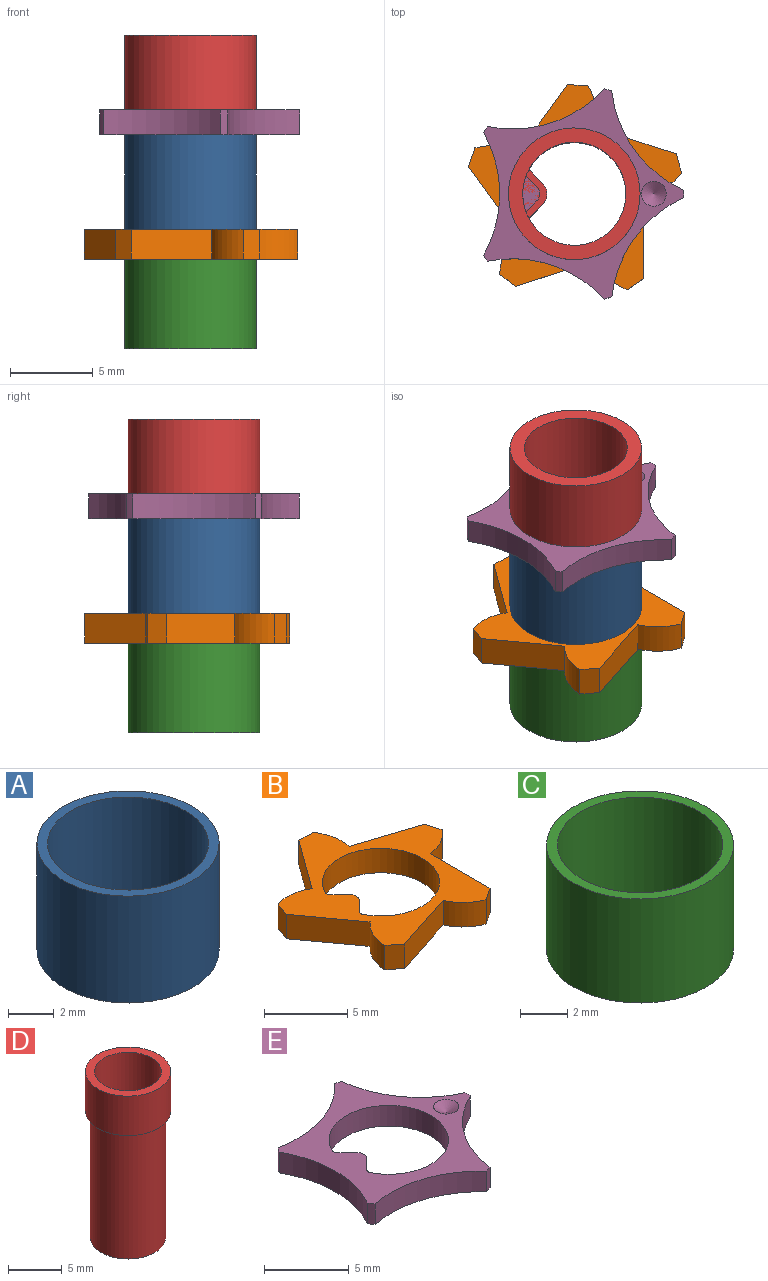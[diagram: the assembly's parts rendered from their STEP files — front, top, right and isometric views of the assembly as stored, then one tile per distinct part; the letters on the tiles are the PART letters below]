
ASSEMBLY  parts=5 mates=3
PART A: 4 faces, bbox 7.9x7.9x5.7 mm
  f0: cylinder r=3.51mm len=7.02mm, axis (0,0,-1), area 125.7mm2, adj f2,f3
  f1: cylinder r=3.97mm len=7.94mm, axis (0,0,-1), area 142.2mm2, adj f2,f3
  f2: plane 7.94x7.94mm, normal (0,0,1), area 10.8mm2, adj f0,f1
  f3: plane 7.94x7.94mm, normal (0,0,-1), area 10.8mm2, adj f0,f1
PART B: 23 faces, bbox 12.9x12.4x1.8 mm
  f0: plane 5.09x1.8mm, normal (1,0,0), area 9.2mm2, adj f1,f20,f21,f22
  f1: cylinder r=3.29mm len=2.28mm, axis (0,0,-1), area 4.8mm2, adj f0,f2,f21,f22
  f2: plane 1.8x1.15mm, normal (0.96,0.28,0), area 2.2mm2, adj f1,f3,f21,f22
  f3: plane 4.84x1.8mm, normal (0.31,0.95,0), area 9.2mm2, adj f2,f4,f21,f22
  f4: cylinder r=3.29mm len=2.56mm, axis (0,0,-1), area 4.8mm2, adj f3,f5,f21,f22
  f5: plane 1.8x1.2mm, normal (0.03,1,0), area 2.2mm2, adj f4,f6,f21,f22
  f6: plane 4.12x2.99mm, normal (-0.81,0.59,0), area 9.2mm2, adj f5,f7,f21,f22
  f7: cylinder r=3.29mm len=2.59mm, axis (0,0,-1), area 4.8mm2, adj f6,f8,f21,f22
  f8: plane 1.8x1.13mm, normal (-0.94,0.34,0), area 2.2mm2, adj f7,f9,f21,f22
  f9: plane 4.12x2.99mm, normal (-0.81,-0.59,0), area 9.2mm2, adj f8,f10,f21,f22
  f10: cylinder r=3.29mm len=2.37mm, axis (0,0,-1), area 4.8mm2, adj f9,f11,f21,f22
  f11: plane 1.8x0.95mm, normal (-0.61,-0.79,0), area 2.2mm2, adj f10,f12,f21,f22
  f12: plane 4.84x1.8mm, normal (0.31,-0.95,0), area 9.2mm2, adj f11,f13,f21,f22
  f13: cylinder r=3.29mm len=1.91mm, axis (0,0,-1), area 4.8mm2, adj f12,f20,f21,f22
  f14: cylinder r=3.53mm len=7.06mm, axis (0,0,-1), area 33.9mm2, adj f15,f19,f21,f22
  f15: cylinder r=0.3mm len=1.8mm, axis (0,0,-1), area 0.7mm2, adj f14,f16,f21,f22
  f16: plane 1.8x0.83mm, normal (0.71,-0.71,0), area 2.1mm2, adj f15,f17,f21,f22
  f17: cylinder r=0.6mm len=1.8mm, axis (0,0,-1), area 1.7mm2, adj f16,f18,f21,f22
  f18: plane 1.8x0.83mm, normal (0.71,0.71,0), area 2.1mm2, adj f17,f19,f21,f22
  f19: cylinder r=0.3mm len=1.8mm, axis (0,0,-1), area 0.7mm2, adj f14,f18,f21,f22
  f20: plane 1.8x0.99mm, normal (0.56,-0.83,0), area 2.2mm2, adj f0,f13,f21,f22
  f21: plane 12.87x12.36mm, normal (0,0,1), area 52.2mm2, adj f0,f1,f2,f3,f4,f5,f6,f7
  f22: plane 12.87x12.36mm, normal (0,0,-1), area 52.2mm2, adj f0,f1,f2,f3,f4,f5,f6,f7
PART C: 4 faces, bbox 7.9x7.9x5.4 mm
  f0: cylinder r=3.51mm len=7.02mm, axis (0,0,-1), area 119.1mm2, adj f2,f3
  f1: cylinder r=3.97mm len=7.94mm, axis (0,0,-1), area 134.7mm2, adj f2,f3
  f2: plane 7.94x7.94mm, normal (0,0,1), area 10.8mm2, adj f0,f1
  f3: plane 7.94x7.94mm, normal (0,0,-1), area 10.8mm2, adj f0,f1
PART D: 12 faces, bbox 7.9x7.9x18.9 mm
  f0: cylinder r=3.11mm len=18.9mm, axis (0,0,-1), area 321.8mm2, adj f2,f4,f6,f7,f11
  f1: cylinder r=3.97mm len=7.94mm, axis (0,0,-1), area 112.2mm2, adj f2,f3
  f2: plane 7.94x7.94mm, normal (0,0,1), area 19.2mm2, adj f0,f1
  f3: plane 7.94x7.94mm, normal (0,0,-1), area 10.8mm2, adj f1,f10
  f4: plane 3.13x1.46mm, normal (0,0,1), area 2.7mm2, adj f0,f5,f6,f7,f8,f9
  f5: plane 14.4x0.75mm, normal (0.71,-0.71,0), area 15.2mm2, adj f4,f6,f9,f11
  f6: cylinder r=0.15mm len=14.4mm, axis (0,0,1), area 2.8mm2, adj f0,f4,f5,f11
  f7: cylinder r=0.15mm len=14.4mm, axis (0,0,1), area 2.8mm2, adj f0,f4,f8,f11
  f8: plane 14.4x0.75mm, normal (0.71,0.71,0), area 15.2mm2, adj f4,f7,f9,f11
  f9: cylinder r=0.9mm len=14.4mm, axis (0,0,1), area 20.4mm2, adj f4,f5,f8,f11
  f10: cylinder r=3.51mm len=14.4mm, axis (0,0,1), area 317.5mm2, adj f3,f11
  f11: plane 7.02x7.02mm, normal (0,0,-1), area 11mm2, adj f0,f5,f6,f7,f8,f9,f10
PART E: 19 faces, bbox 12.1x12.7x1.5 mm
  f0: cylinder r=7.5mm len=7.03mm, axis (0,0,-1), area 11.6mm2, adj f1,f15,f16,f17
  f1: cylinder r=6.6mm len=1.5mm, axis (0,0,-1), area 0.7mm2, adj f0,f2,f16,f17
  f2: cylinder r=7.5mm len=7.39mm, axis (0,0,-1), area 11.6mm2, adj f1,f3,f16,f17
  f3: cylinder r=6.6mm len=1.5mm, axis (0,0,-1), area 0.7mm2, adj f2,f4,f16,f17
  f4: cylinder r=7.5mm len=7.02mm, axis (0,0,-1), area 11.6mm2, adj f3,f5,f16,f17
  f5: cylinder r=6.6mm len=1.5mm, axis (0,0,-1), area 0.7mm2, adj f4,f6,f16,f17
  f6: cylinder r=7.5mm len=5.97mm, axis (0,0,-1), area 11.6mm2, adj f5,f7,f16,f17
  f7: cylinder r=6.6mm len=1.5mm, axis (0,0,-1), area 0.7mm2, adj f6,f8,f16,f17
  f8: cylinder r=7.5mm len=5.98mm, axis (0,0,-1), area 11.6mm2, adj f7,f15,f16,f17
  f9: cylinder r=3.53mm len=7.06mm, axis (0,0,-1), area 28.3mm2, adj f10,f14,f16,f17
  f10: cylinder r=0.3mm len=1.5mm, axis (0,0,-1), area 0.6mm2, adj f9,f11,f16,f17
  f11: plane 1.5x0.83mm, normal (0.71,-0.71,0), area 1.8mm2, adj f10,f12,f16,f17
  f12: cylinder r=0.6mm len=1.5mm, axis (0,0,-1), area 1.4mm2, adj f11,f13,f16,f17
  f13: plane 1.5x0.83mm, normal (0.71,0.71,0), area 1.8mm2, adj f12,f14,f16,f17
  f14: cylinder r=0.3mm len=1.5mm, axis (0,0,-1), area 0.6mm2, adj f9,f13,f16,f17
  f15: cylinder r=6.6mm len=1.5mm, axis (0,0,-1), area 0.7mm2, adj f0,f8,f16,f17
  f16: plane 12.69x12.07mm, normal (0,0,1), area 45.8mm2, adj f0,f1,f2,f3,f4,f5,f6,f7
  f17: plane 12.69x12.07mm, normal (0,0,-1), area 47.6mm2, adj f0,f1,f2,f3,f4,f5,f6,f7
  f18: cone r=0.75mm half-angle=60deg, axis (0,0,1), area 2mm2, adj f16
PLACE A t=(0,0,-1.2)mm
PLACE B t=(0,0,-3)mm
PLACE C t=(0,0,-8.4)mm
PLACE D t=(0,0,6)mm
PLACE E t=(0,0,4.5)mm
MATE fastened B.f14 <-> C.f0  axis (0,0,-1) through (0,0,-3)mm
MATE fastened A.f0 <-> E.f1  axis (0,0,-1) through (0,0,4.5)mm
MATE fastened A.f0 <-> B.f14  axis (0,0,-1) through (0,0,-1.2)mm
